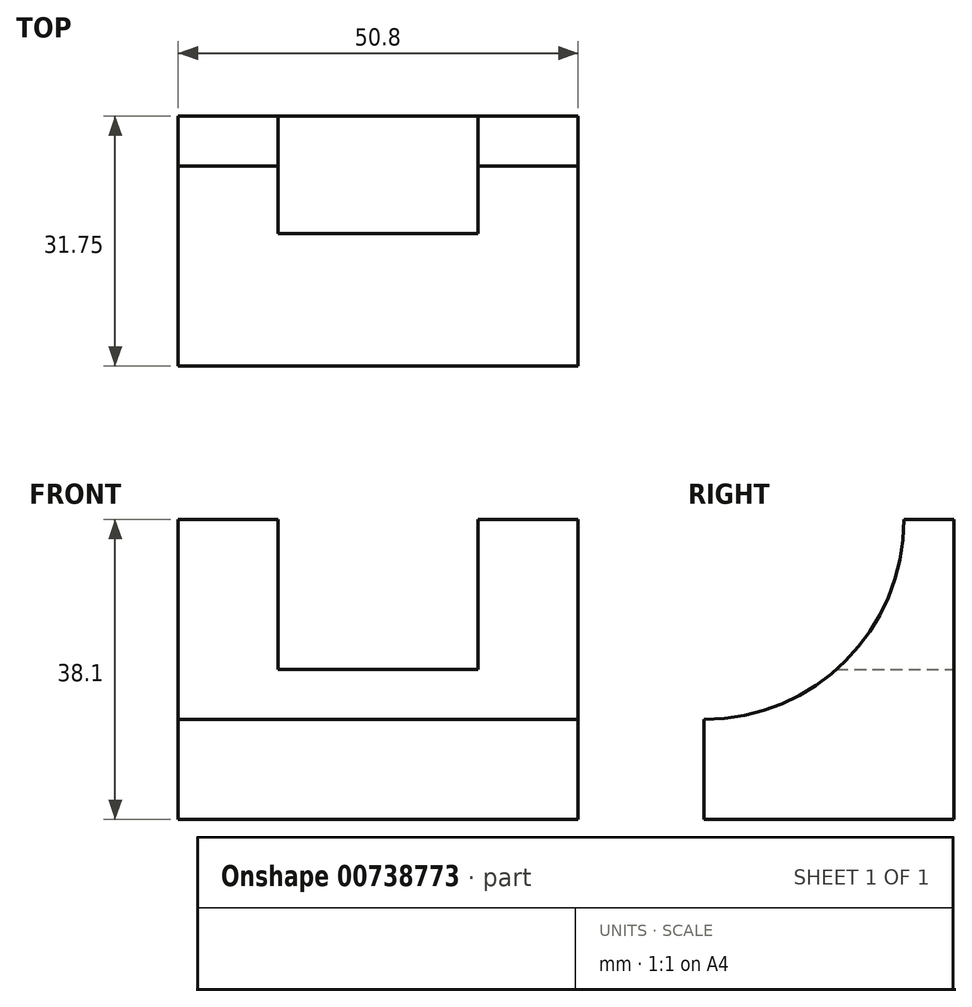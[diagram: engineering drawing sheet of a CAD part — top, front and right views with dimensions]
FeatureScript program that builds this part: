
annotation { "Feature Type Name" : "Feature", "Feature Type Description" : "" }
export const myFeature = defineFeature(function(context is Context, id is Id, definition is map)
    precondition{}
    {
        {
            var Q0;
            Q0=qCreatedBy(makeId("Front.planeOp"),FACE);
            var sketch = newSketch(context, id + "F0", { "sketchPlane" : qUnion([Q0])});
            skLineSegment(sketch, "E0", {"start": v(0, 0) * mm, "end": v(0, 38.1) * mm});
            skLineSegment(sketch, "E1", {"start": v(0, 38.1) * mm, "end": v(50.8, 38.1) * mm});
            skLineSegment(sketch, "E2", {"start": v(50.8, 38.1) * mm, "end": v(50.8, 0) * mm});
            skLineSegment(sketch, "E3", {"start": v(50.8, 0) * mm, "end": v(0, 0) * mm});
            skSolve(sketch);
        }
        {
            var Q0;
            Q0 = qSketchRegion(id + "F0", true);
            extrude(context, id + "F1", {"entities" : qUnion([Q0]), "depth" : 31.75 * mm, "offsetDistance" : 25.4 * mm});
        }
        {
            var Q0;
            Q0=qCreatedBy(makeId("Front.planeOp"),FACE);
            var sketch = newSketch(context, id + "F2", { "sketchPlane" : qUnion([Q0])});
            skLineSegment(sketch, "E4", {"start": v(0, 19.05) * mm, "end": v(50.8, 19.05) * mm});
            skLineSegment(sketch, "E5", {"start": v(12.7, 38.1) * mm, "end": v(12.7, 19.05) * mm});
            skLineSegment(sketch, "E6", {"start": v(38.1, 38.1) * mm, "end": v(38.1, 19.05) * mm});
            skLineSegment(sketch, "E7", {"start": v(12.7, 38.1) * mm, "end": v(38.1, 38.1) * mm});
            skSolve(sketch);
        }
        {
            var Q0;
            Q0 = qSketchRegion(id + "F2", true);
            extrude(context, id + "F3", {"entities" : qUnion([Q0]), "operationType" : NewBodyOperationType.REMOVE, "endBound" : BoundingType.THROUGH_ALL, "depth" : 25.4 * mm, "offsetDistance" : 25.4 * mm});
        }
        {
            var Q0;
            Q0=qCreatedBy(makeId("Right.planeOp"),FACE);
            var sketch = newSketch(context, id + "F4", { "sketchPlane" : qUnion([Q0])});
            skArc(sketch, "E8", {"start": v(-31.75, 12.7) * mm, "mid": v(-13.79, 20.14) * mm, "end": v(-6.35, 38.1) * mm});
            skLineSegment(sketch, "E9", {"start": v(-31.75, 12.7) * mm, "end": v(-31.75, 38.1) * mm});
            skPoint(sketch, "E10.end.orphan", {"position": v(0, 12.7) * mm});
            skPoint(sketch, "E11.end.orphan", {"position": v(-6.35, 0) * mm});
            skLineSegment(sketch, "E12", {"start": v(-31.75, 38.1) * mm, "end": v(-6.35, 38.1) * mm});
            skSolve(sketch);
        }
        {
            var Q0;
            Q0 = qSketchRegion(id + "F4", true);
            extrude(context, id + "F5", {"entities" : qUnion([Q0]), "operationType" : NewBodyOperationType.REMOVE, "endBound" : BoundingType.THROUGH_ALL, "depth" : 25.4 * mm, "offsetDistance" : 25.4 * mm});
        }
    });
